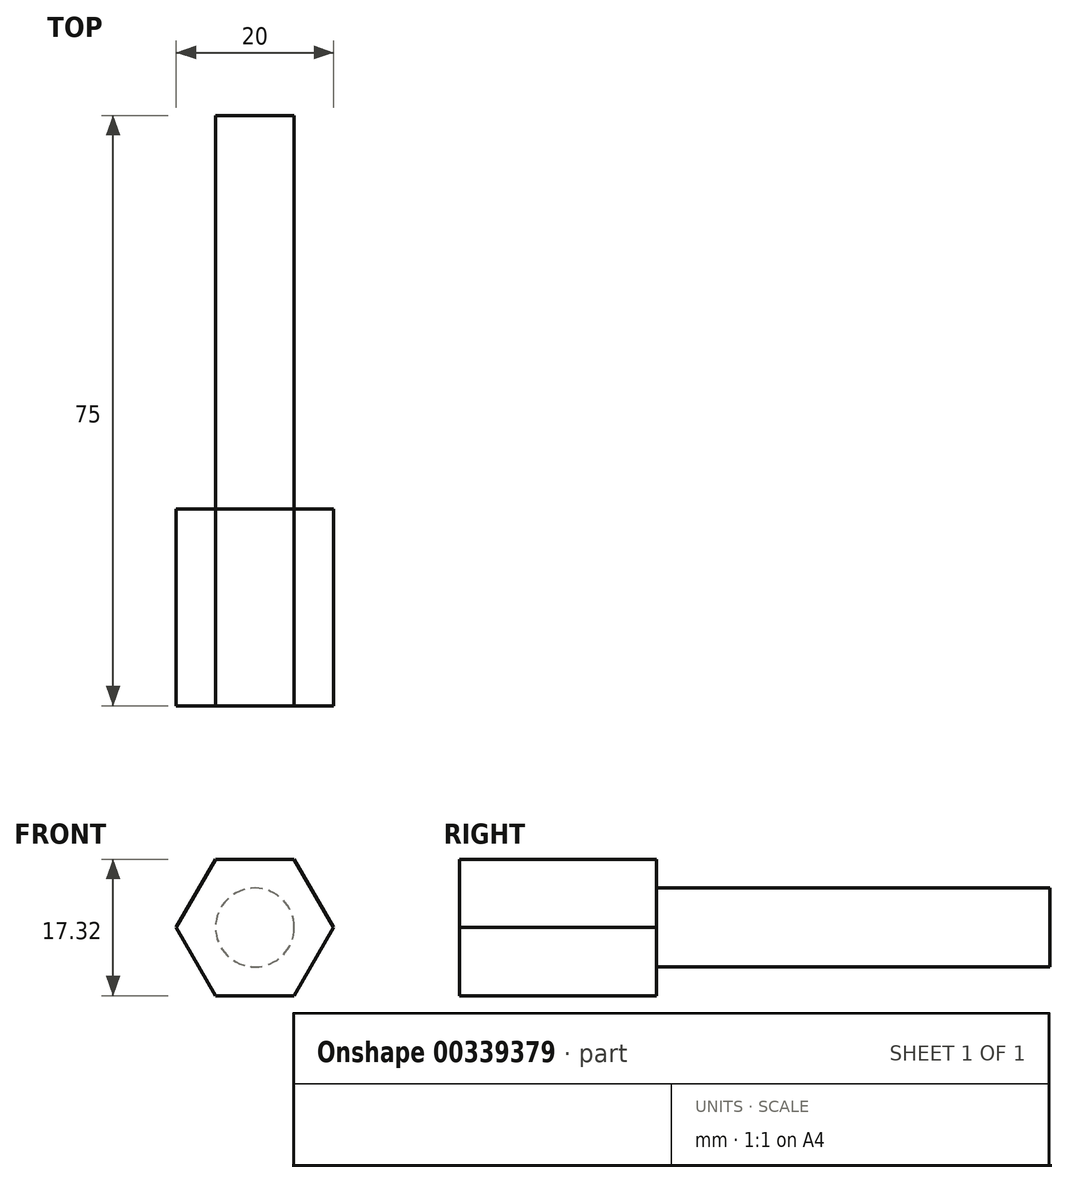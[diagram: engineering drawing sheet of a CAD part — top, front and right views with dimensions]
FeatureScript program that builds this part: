
annotation { "Feature Type Name" : "Feature", "Feature Type Description" : "" }
export const myFeature = defineFeature(function(context is Context, id is Id, definition is map)
    precondition{}
    {
        {
            var Q0;
            Q0=qCreatedBy(makeId("Front.planeOp"),FACE);
            var sketch = newSketch(context, id + "F0", { "sketchPlane" : qUnion([Q0])});
            skLineSegment(sketch, "E0.bottom", {"start": v(5, 8.66) * mm, "end": v(-5, 8.66) * mm});
            skLineSegment(sketch, "E0.top", {"start": v(5, -8.66) * mm, "end": v(-5, -8.66) * mm});
            skLineSegment(sketch, "E0.left", {"start": v(5, 8.66) * mm, "end": v(5, -8.66) * mm});
            skLineSegment(sketch, "E0.right", {"start": v(-5, 8.66) * mm, "end": v(-5, -8.66) * mm});
            skPoint(sketch, "E0.middle", {"position": v(0, 0) * mm});
            skLineSegment(sketch, "E1", {"start": v(5, 8.66) * mm, "end": v(10, 0) * mm});
            skLineSegment(sketch, "E2", {"start": v(10, 0) * mm, "end": v(5, -8.66) * mm});
            skLineSegment(sketch, "E3", {"start": v(-5, -8.66) * mm, "end": v(-10, 0) * mm});
            skLineSegment(sketch, "E4", {"start": v(-10, 0) * mm, "end": v(-5, 8.66) * mm});
            skCircle(sketch, "E5", {"center": v(0, 0) * mm, "radius": 5 * mm});
            skSolve(sketch);
        }
        {
            var Q0;
            {var subQ3=sQuery(id+"F0.wireOp",EDGE,"E3");Q0=makeQuery(id+"F0.imprint","IMPRINT",FACE,{"disambiguationData":[TD([[makeQuery(id+"F0.imprint","IMPRINT",EDGE,{"derivedFrom":subQ3}),-1.0]])]});}
            var Q1;
            {var subQ0=sQuery(id+"F0.wireOp",EDGE,"E0.top");Q1=makeQuery(id+"F0.imprint","IMPRINT",FACE,{"disambiguationData":[TD([[makeQuery(id+"F0.imprint","IMPRINT",EDGE,{"derivedFrom":subQ0}),-1.0]])]});}
            var Q2;
            {var subQ0=sQuery(id+"F0.wireOp",EDGE,"E5");var subQ1=makeQuery(id+"F0.imprint","INTERSECT",VERTEX,{"derivedFrom":[sQuery(id+"F0.wireOp",EDGE,"E0.left"),subQ0]});Q2=makeQuery(id+"F0.imprint","IMPRINT",FACE,{"disambiguationData":[TD([[makeQuery(id+"F0.imprint","IMPRINT",EDGE,{"disambiguationData":[TD([[subQ1,-1.0]])],"derivedFrom":subQ0}),1.0]])]});}
            var Q3;
            {var subQ0=sQuery(id+"F0.wireOp",EDGE,"E0.bottom");Q3=makeQuery(id+"F0.imprint","IMPRINT",FACE,{"disambiguationData":[TD([[makeQuery(id+"F0.imprint","IMPRINT",EDGE,{"derivedFrom":subQ0}),1.0]])]});}
            var Q4;
            {var subQ0=sQuery(id+"F0.wireOp",EDGE,"E1");Q4=makeQuery(id+"F0.imprint","IMPRINT",FACE,{"disambiguationData":[TD([[makeQuery(id+"F0.imprint","IMPRINT",EDGE,{"derivedFrom":subQ0}),-1.0]])]});}
            extrude(context, id + "F1", {"entities" : qUnion([Q0, Q1, Q2, Q3, Q4]), "depth" : 25 * mm});
        }
        {
            var Q0;
            {var subQ0=sQuery(id+"F0.wireOp",EDGE,"E5");var subQ1=makeQuery(id+"F0.imprint","INTERSECT",VERTEX,{"derivedFrom":[sQuery(id+"F0.wireOp",EDGE,"E0.left"),subQ0]});Q0=makeQuery(id+"F0.imprint","IMPRINT",FACE,{"disambiguationData":[TD([[makeQuery(id+"F0.imprint","IMPRINT",EDGE,{"disambiguationData":[TD([[subQ1,-1.0]])],"derivedFrom":subQ0}),1.0]])]});}
            extrude(context, id + "F2", {"entities" : qUnion([Q0]), "operationType" : NewBodyOperationType.ADD, "depth" : -50 * mm});
        }
    });
